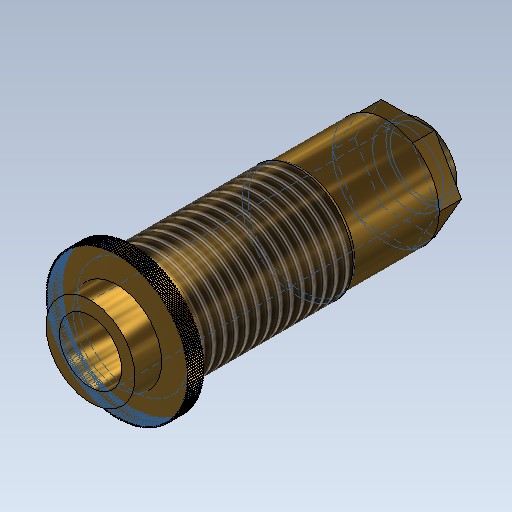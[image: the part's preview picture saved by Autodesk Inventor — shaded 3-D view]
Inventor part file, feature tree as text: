
AUTODESK INVENTOR PART (.ipt)
format: ipt  version: 2020 (Build 240168000, 168)  size: 1,386,496 bytes
history: native  units: mm
features: extrude x11, sketch x11, other x1, fillet x1, thread x1, projected_geometry x1
ambient origin geometry x8: Origin, YZ Plane, XZ Plane, XY Plane, X Axis, Y Axis, Z Axis, Center Point
bodies: Body1 (feature_tree)
feature tree (26):
  other  "ソリッド1"
  extrude  "押し出し1"  Depth=11.0mm
  extrude  "押し出し2"  Depth=2.5mm TaperAngle=0.0deg
  extrude  "押し出し3"  Depth=12.0mm
  extrude  "押し出し4"  Depth=9.5mm TaperAngle=0.0deg
  extrude  "押し出し5"  Depth=12.5mm
  extrude  "押し出し6"  Depth=18.95mm TaperAngle=0.0deg
  extrude  "押し出し7"  Depth=16.0mm
  extrude  "押し出し8"  Depth=1.75mm TaperAngle=0.0deg
  extrude  "押し出し9"  Depth=2.5mm TaperAngle=0.0deg
  extrude  "押し出し11"  Depth=2.5mm TaperAngle=0.0deg
  extrude  "押し出し12"  Depth=7.0mm
  fillet  "フィレット1"  Radius=7.0mm
  thread  "ねじ5"
  sketch  "スケッチ1"
  sketch  "スケッチ2"
  sketch  "スケッチ3"
  sketch  "スケッチ4"
  sketch  "スケッチ5"
  sketch  "スケッチ6"
  projected_geometry  "投影ループ1"
  sketch  "スケッチ8"
  sketch  "スケッチ9"
  sketch  "スケッチ11"
  sketch  "スケッチ12"
  sketch  "スケッチ13"
